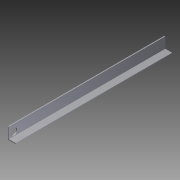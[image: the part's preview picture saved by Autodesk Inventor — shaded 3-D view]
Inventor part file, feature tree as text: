
AUTODESK INVENTOR PART (.ipt)
format: ipt  version: 2012 (Build 160160000, 160)  size: 84,992 bytes
history: native  units: in
note: dims shown in document units (in); Inventor stores cm internally (conversion verified against a paired STEP export)
features: extrude x2, sketch x2
ambient origin geometry x8: Origin, YZ Plane, XZ Plane, XY Plane, X Axis, Y Axis, Z Axis, Center Point
bodies: Solid1 (feature_tree)
feature tree (4):
  extrude  "Extrusion1"  Depth=1.0in
  extrude  "Extrusion2"  Depth=0.125in
  sketch  "Sketch1"  dims[d0=1.5in d1=1.0in]
  sketch  "Sketch2"  dims[d2=0.125in d3=0.125in d4=20.0in d5=0.0in d6=0.875in d7=0.625in d8=0.625in d11=20.0in d12=0.0in]
